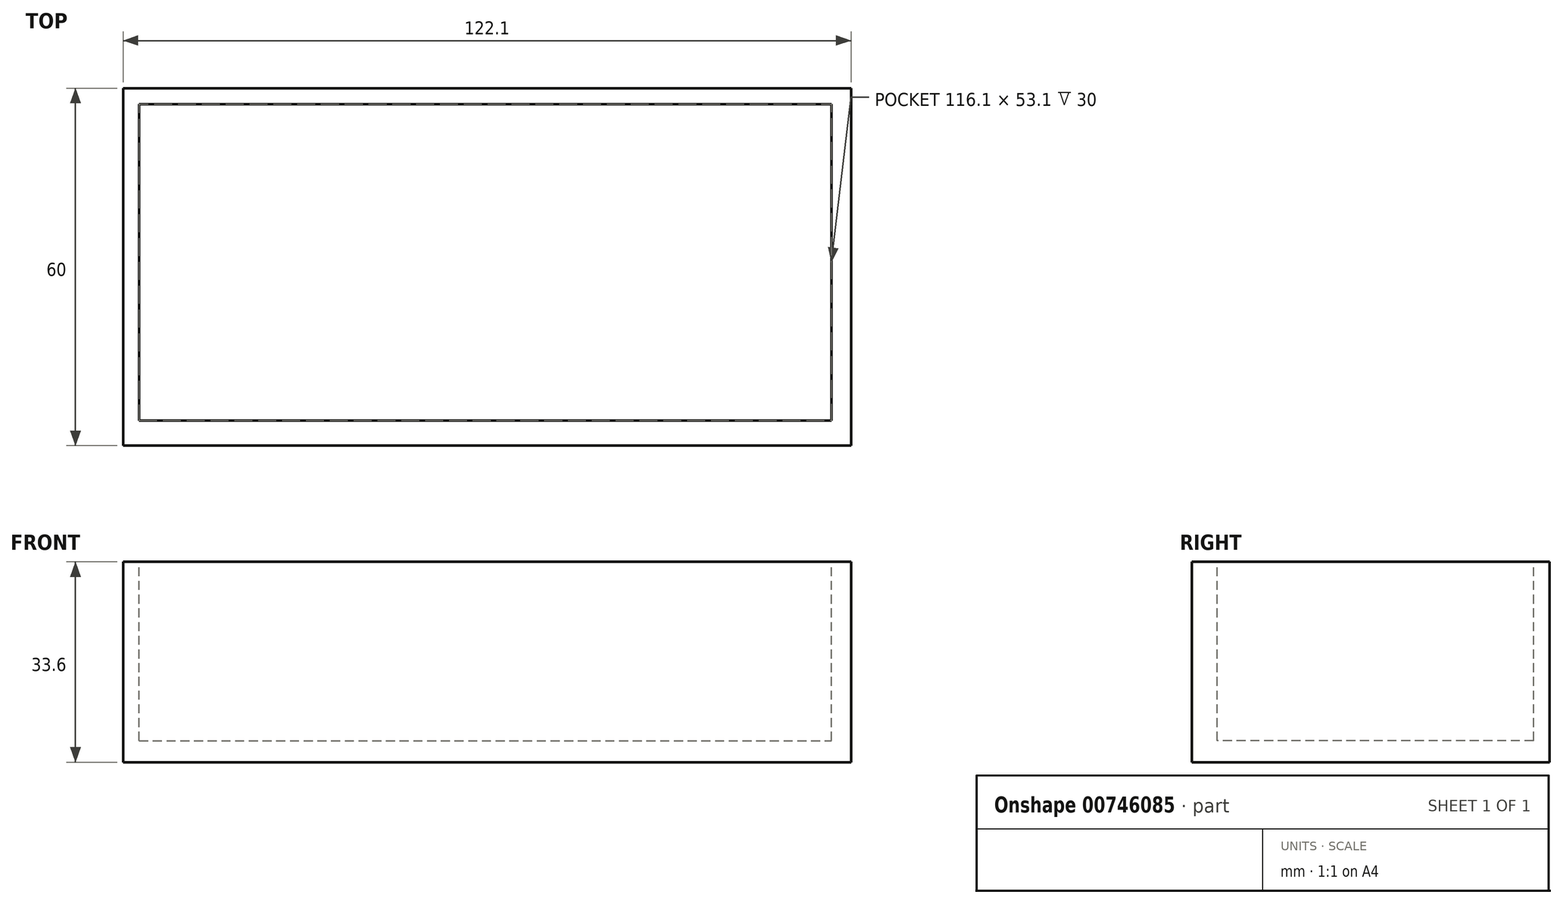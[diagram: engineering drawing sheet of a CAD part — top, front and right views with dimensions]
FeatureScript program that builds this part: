
annotation { "Feature Type Name" : "Feature", "Feature Type Description" : "" }
export const myFeature = defineFeature(function(context is Context, id is Id, definition is map)
    precondition{}
    {
        {
            var Q0;
            Q0=qCreatedBy(makeId("Front.planeOp"),FACE);
            var sketch = newSketch(context, id + "F0", { "sketchPlane" : qUnion([Q0])});
            skLineSegment(sketch, "E0.bottom", {"start": v(-57.45, 6.3) * mm, "end": v(64.65, 6.3) * mm});
            skLineSegment(sketch, "E0.top", {"start": v(-57.45, -27.3) * mm, "end": v(64.65, -27.3) * mm});
            skLineSegment(sketch, "E0.left", {"start": v(-57.45, 6.3) * mm, "end": v(-57.45, -27.3) * mm});
            skLineSegment(sketch, "E0.right", {"start": v(64.65, 6.3) * mm, "end": v(64.65, -27.3) * mm});
            skSolve(sketch);
        }
        {
            var Q0;
            Q0 = qSketchRegion(id + "F0", true);
            extrude(context, id + "F1", {"entities" : qUnion([Q0]), "depth" : 60 * mm, "offsetDistance" : 25 * mm});
        }
        {
            var Q0;
            Q0=makeQuery(id+"F1.opExtrude","SWEPT_FACE",FACE,{"disambiguationData":[OSD([sQuery(id+"F0.wireOp",EDGE,"E0.bottom")])]});
            var sketch = newSketch(context, id + "F2", { "sketchPlane" : qUnion([Q0])});
            skLineSegment(sketch, "E1.bottom", {"start": v(-54.75, -2.7) * mm, "end": v(61.35, -2.7) * mm});
            skLineSegment(sketch, "E1.top", {"start": v(-54.75, -55.8) * mm, "end": v(61.35, -55.8) * mm});
            skLineSegment(sketch, "E1.left", {"start": v(-54.75, -2.7) * mm, "end": v(-54.75, -55.8) * mm});
            skLineSegment(sketch, "E1.right", {"start": v(61.35, -2.7) * mm, "end": v(61.35, -55.8) * mm});
            skSolve(sketch);
        }
        {
            var Q0;
            Q0=makeQuery(id+"F2.imprint","IMPRINT",FACE,{"disambiguationData":[TD([[makeQuery(id+"F2.imprint","IMPRINT",EDGE,{"derivedFrom":sQuery(id+"F2.wireOp",EDGE,"E1.bottom")}),-1.0]])]});
            extrude(context, id + "F3", {"entities" : qUnion([Q0]), "operationType" : NewBodyOperationType.REMOVE, "oppositeDirection" : true, "depth" : 30 * mm, "offsetDistance" : 25 * mm});
        }
    });
